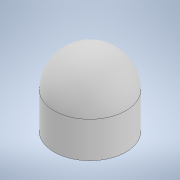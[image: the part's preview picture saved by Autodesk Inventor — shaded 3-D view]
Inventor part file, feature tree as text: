
AUTODESK INVENTOR PART (.ipt)
format: ipt  version: 2020.2 (Build 242310000, 310)  size: 125,440 bytes
history: native  units: mm
features: extrude x2, sketch x2, fillet x1
ambient origin geometry x8: Origin, YZ Plane, XZ Plane, XY Plane, X Axis, Y Axis, Z Axis, Center Point
bodies: Solid1 (feature_tree), Solid2 (feature_tree)
feature tree (5):
  extrude  "Extrusion1"  Depth=20.0mm
  extrude  "Extrusion2"  Depth=50.0mm
  fillet  "Fillet1"  Radius=100.0mm
  sketch  "Sketch1"  dims[d1=20.0mm d2=0.0mm d6=20.0mm]
  sketch  "Sketch2"  dims[d7=20.0mm d8=100.0mm d9=100.0mm d10=0.0mm d11=50.0mm d12=0.5mm d13=0.872665mm d14=0.5mm d15=0.872665mm]
